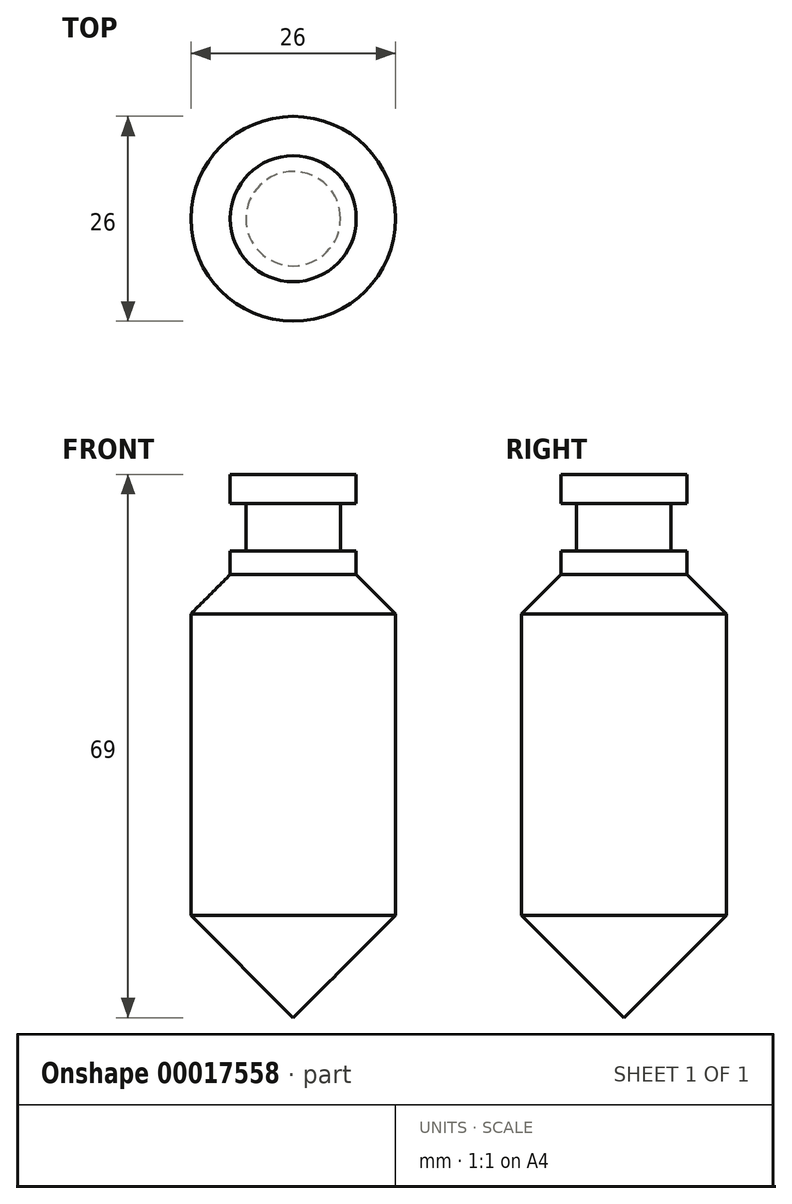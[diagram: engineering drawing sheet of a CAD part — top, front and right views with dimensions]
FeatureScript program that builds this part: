
annotation { "Feature Type Name" : "Feature", "Feature Type Description" : "" }
export const myFeature = defineFeature(function(context is Context, id is Id, definition is map)
    precondition{}
    {
        {
            var Q0;
            Q0=qCreatedBy(makeId("Top.planeOp"),FACE);
            var sketch = newSketch(context, id + "F0", { "sketchPlane" : qUnion([Q0])});
            skCircle(sketch, "E0", {"center": v(0, 0) * mm, "radius": 8 * mm});
            skSolve(sketch);
        }
        {
            var Q0;
            Q0=qSketchRegion(id+"F0",true);
            extrude(context, id + "F1", {"entities" : qUnion([Q0]), "depth" : 3.7 * mm});
        }
        {
            var Q0;
            Q0=makeQuery(id+"F1.opExtrude","CAP_FACE",FACE,{"disambiguationData":[OSD([sQuery(id+"F0.wireOp",EDGE,"E0")])],"isStart":true});
            var sketch = newSketch(context, id + "F2", { "sketchPlane" : qUnion([Q0])});
            skCircle(sketch, "E1", {"center": v(0, 0) * mm, "radius": 6 * mm});
            skSolve(sketch);
        }
        {
            var Q0;
            Q0=qSketchRegion(id+"F2",true);
            extrude(context, id + "F3", {"entities" : qUnion([Q0]), "operationType" : NewBodyOperationType.ADD, "depth" : 6 * mm});
        }
        {
            var Q0;
            Q0=makeQuery(id+"F3.opExtrude","CAP_FACE",FACE,{"disambiguationData":[OSD([sQuery(id+"F2.wireOp",EDGE,"E1")])],"isStart":false});
            var sketch = newSketch(context, id + "F4", { "sketchPlane" : qUnion([Q0])});
            skCircle(sketch, "E2", {"center": v(0, 0) * mm, "radius": 8 * mm});
            skSolve(sketch);
        }
        {
            var Q0;
            Q0=qSketchRegion(id+"F4",true);
            extrude(context, id + "F5", {"entities" : qUnion([Q0]), "operationType" : NewBodyOperationType.ADD, "depth" : 3 * mm});
        }
        {
            var Q0;
            Q0=makeQuery(id+"F5.opExtrude","CAP_FACE",FACE,{"disambiguationData":[OSD([sQuery(id+"F4.wireOp",EDGE,"E2")])],"isStart":false});
            var sketch = newSketch(context, id + "F6", { "sketchPlane" : qUnion([Q0])});
            skCircle(sketch, "E3", {"center": v(0, 0) * mm, "radius": 13 * mm});
            skSolve(sketch);
        }
        {
            var Q0;
            Q0=qSketchRegion(id+"F6",true);
            extrude(context, id + "F7", {"entities" : qUnion([Q0]), "operationType" : NewBodyOperationType.ADD, "depth" : 56.3 * mm});
        }
        {
            var Q0;
            Q0=makeQuery(id+"F7.opExtrude","CAP_EDGE",EDGE,{"disambiguationData":[OSD([sQuery(id+"F6.wireOp",EDGE,"E3")])],"isStart":false});
            chamfer(context, id + "F8", {"entities" : qUnion([Q0]), "width" : 13 * mm, "tangentPropagation" : true});
        }
        {
            var Q0;
            Q0=makeQuery(id+"F7.opExtrude","CAP_EDGE",EDGE,{"disambiguationData":[OSD([sQuery(id+"F6.wireOp",EDGE,"E3")])],"isStart":true});
            chamfer(context, id + "F9", {"entities" : qUnion([Q0]), "width" : 5 * mm, "tangentPropagation" : true});
        }
    });
